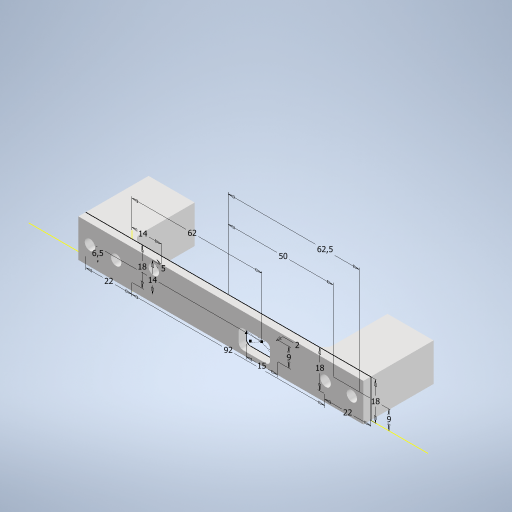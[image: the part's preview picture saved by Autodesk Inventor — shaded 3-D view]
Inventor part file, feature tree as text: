
AUTODESK INVENTOR PART (.ipt)
format: ipt  version: 2024.3 (Build 283343000, 343)  size: 281,088 bytes
history: native  units: in
note: dims shown in document units (in); Inventor stores cm internally (conversion verified against a paired STEP export)
features: extrude x2, sketch x1, hole x1, fillet x1
ambient origin geometry x8: Origin, YZ Plane, XZ Plane, XY Plane, X Axis, Y Axis, Z Axis, Center Point
bodies: Body1 (feature_tree)
feature tree (5):
  sketch  "Sketch3"  dims[d26=0.1969in d29=0.5906in d30=0.3543in d31=0.0787in d34=3.622in d35=0.7087in d36=0.8661in d37=0.7087in d38=0.8661in d39=0.7087in d41=0.5512in d42=0.5512in d44=0.1378in d45=0.0in d46=1.1811in d47=0.0in d48=0.1969in d49=0.2362in d50=0.1575in d51=0.0787in d52=90.0deg d53=0.315in d54=0.8108in d55=0.1575in d56=2.4409in d57=0.2559in d60=1.9685in d61=2.4606in d62=0.3543in]
  extrude  "Extrusion4"  Depth=3.622in
  extrude  "Extrusion5"  Depth=0.7087in
  hole  "Hole1"  [1 undecoded]
  fillet  "Fillet1"  Radius=0.7087in
note: 1 required parameter value undecoded (feature->parameter linkage not recoverable at this tier; creation-order binding heuristic only, values carry confidence <= 0.55)
